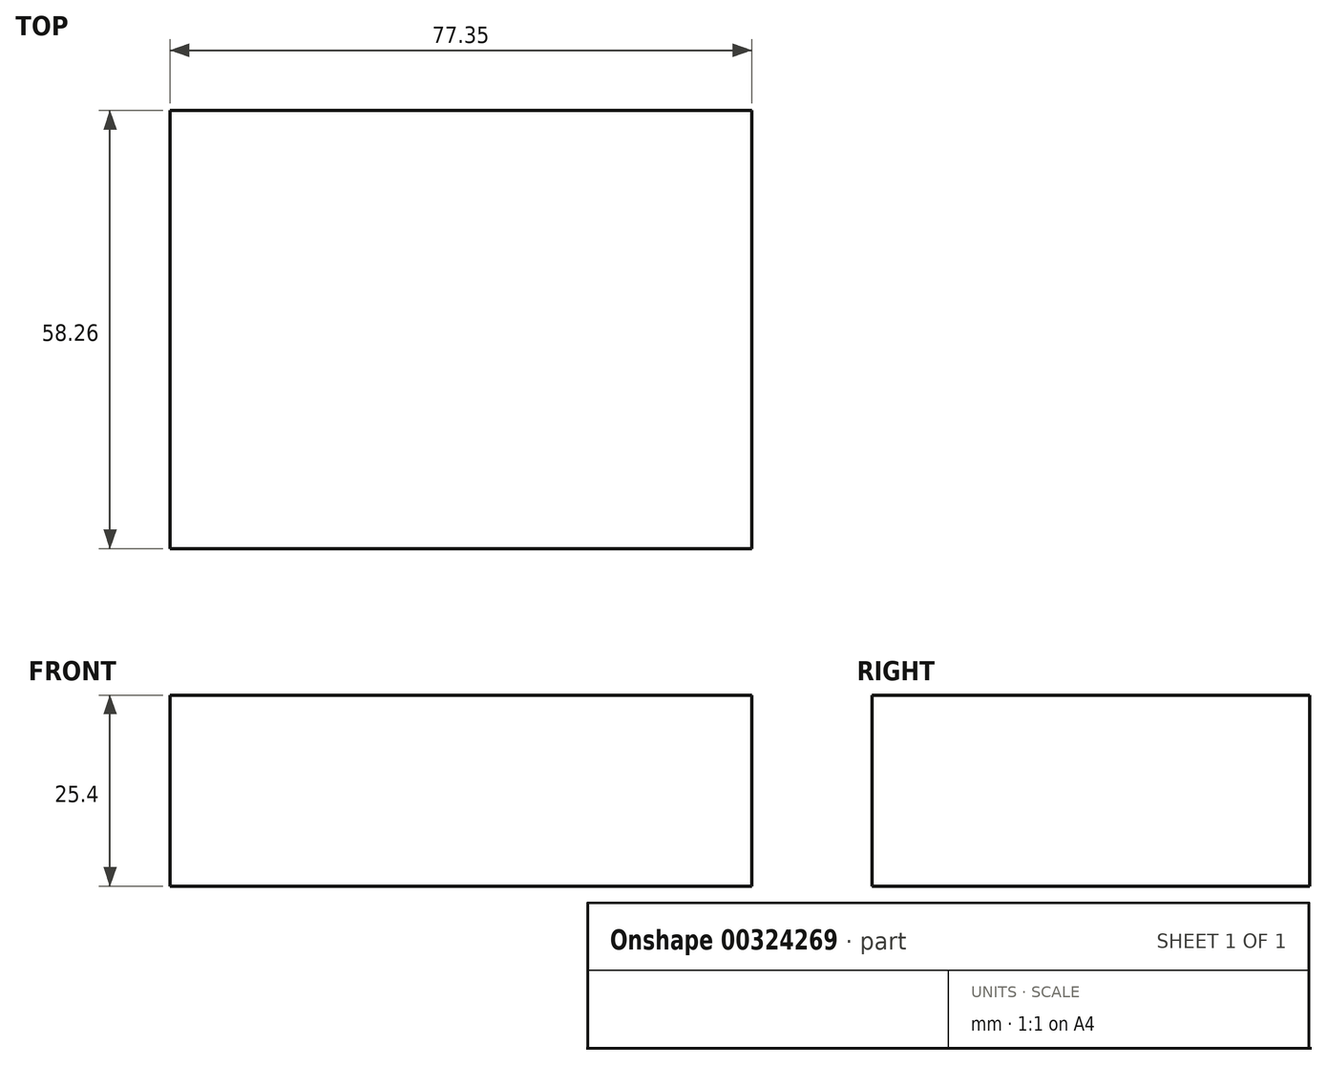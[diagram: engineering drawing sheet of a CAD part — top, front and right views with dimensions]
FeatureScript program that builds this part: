
annotation { "Feature Type Name" : "Feature", "Feature Type Description" : "" }
export const myFeature = defineFeature(function(context is Context, id is Id, definition is map)
    precondition{}
    {
        {
            var Q0;
            Q0=qCreatedBy(makeId("Top.planeOp"),FACE);
            var sketch = newSketch(context, id + "F0", { "sketchPlane" : qUnion([Q0])});
            skLineSegment(sketch, "E0", {"start": v(0, -58.26) * mm, "end": v(77.35, -58.26) * mm});
            skLineSegment(sketch, "E1", {"start": v(77.35, -58.26) * mm, "end": v(77.35, 0) * mm});
            skLineSegment(sketch, "E2", {"start": v(77.35, 0) * mm, "end": v(0, 0) * mm});
            skLineSegment(sketch, "E3", {"start": v(0, 0) * mm, "end": v(0, -58.26) * mm});
            skSolve(sketch);
        }
        {
            var Q0;
            Q0 = qSketchRegion(id + "F0", true);
            extrude(context, id + "F1", {"entities" : qUnion([Q0]), "depth" : 25.4 * mm});
        }
    });
